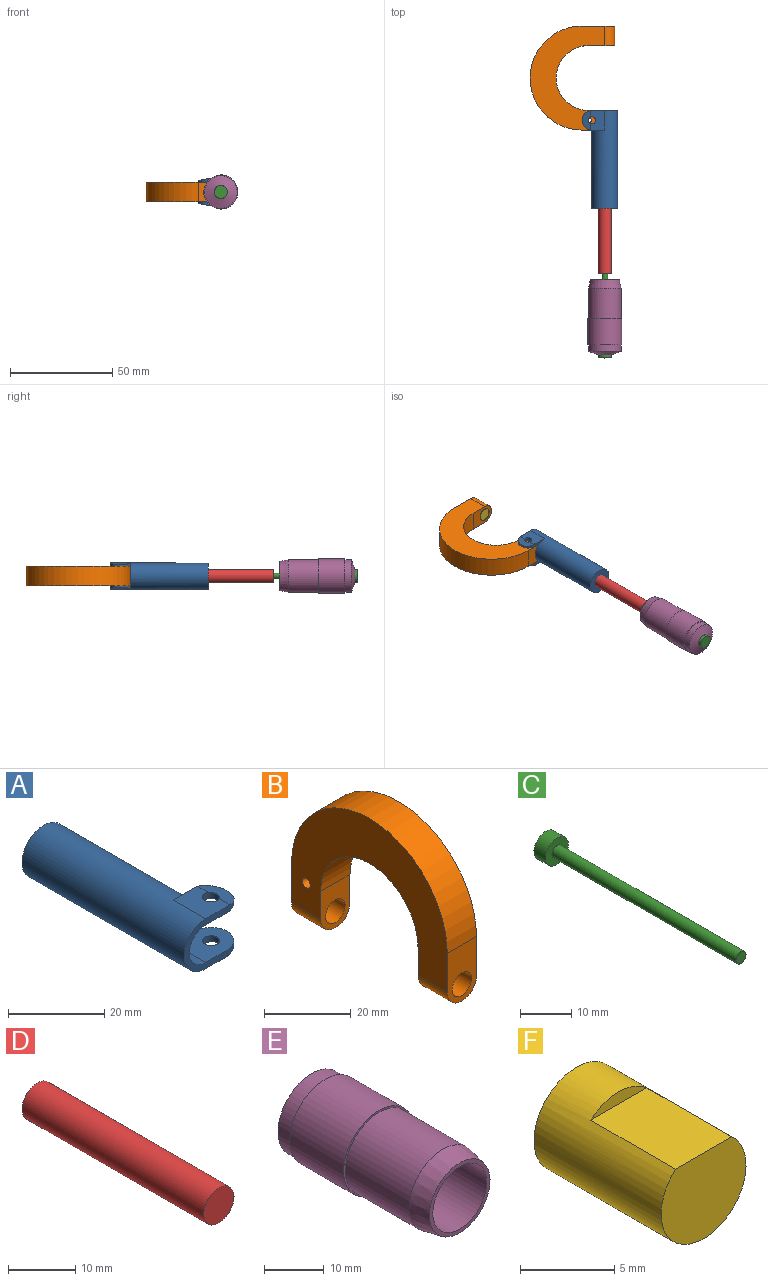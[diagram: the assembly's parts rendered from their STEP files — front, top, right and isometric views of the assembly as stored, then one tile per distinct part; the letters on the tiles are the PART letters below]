
ASSEMBLY  parts=6 mates=6
PART A: 20 faces, bbox 17.5x47.6x12.7 mm
  f0: cylinder r=3.17mm len=31.75mm, axis (0,-1,0), area 633.4mm2, adj f4,f7
  f1: plane 6.35x1.59mm, normal (0,1,0), area 5.5mm2, adj f6,f10,f12,f16
  f2: plane 12.7x12.7mm, normal (0,1,0), area 122.2mm2, adj f3,f6
  f3: cylinder r=1.19mm len=6.35mm, axis (0,-1,0), area 47.5mm2, adj f2,f4
  f4: plane 6.35x6.35mm, normal (0,-1,0), area 27.2mm2, adj f0,f3
  f5: plane 6.35x1.59mm, normal (0,1,0), area 5.5mm2, adj f6,f9,f14,f17
  f6: cylinder r=6.35mm len=47.63mm, axis (0,-1,0), area 1710.1mm2, adj f1,f2,f5,f7,f9,f10,f15
  f7: plane 11.11x9.53mm, normal (0,-1,0), area 58.2mm2, adj f0,f6,f12,f13,f14
  f8: plane 9.4x3.99mm, normal (0.2,0,-0.98), area 26.6mm2, adj f9,f17,f18
  f9: plane 9.53x7.12mm, normal (0,0,-1), area 60.4mm2, adj f5,f6,f8,f15,f17,f18
  f10: plane 9.53x7.12mm, normal (0,0,1), area 60.4mm2, adj f1,f6,f11,f15,f16,f19
  f11: plane 9.4x3.99mm, normal (0.2,0,0.98), area 26.6mm2, adj f10,f16,f19
  f12: plane 11.11x9.53mm, normal (0,0,-1), area 86.5mm2, adj f1,f7,f13,f15,f16,f19
  f13: cylinder r=4.76mm len=9.53mm, axis (0,-1,0), area 142.5mm2, adj f7,f12,f14,f15
  f14: plane 11.11x9.53mm, normal (0,0,1), area 86.5mm2, adj f5,f7,f13,f15,f17,f18
  f15: plane 12.7x12.7mm, normal (0,-1,0), area 47.9mm2, adj f6,f9,f10,f12,f13,f14,f16,f17
  f16: cylinder r=4.76mm len=9.53mm, axis (0,0,-1), area 16.9mm2, adj f1,f10,f11,f12,f15
  f17: cylinder r=4.76mm len=9.53mm, axis (0,0,-1), area 16.9mm2, adj f5,f8,f9,f14,f15
  f18: cylinder r=1.75mm len=3.51mm, axis (0,0,1), area 17mm2, adj f8,f9,f14
  f19: cylinder r=1.75mm len=3.51mm, axis (0,0,1), area 17mm2, adj f10,f11,f12
PART B: 15 faces, bbox 9.5x50.8x41.3 mm
  f0: plane 12.7x9.53mm, normal (0,-1,0), area 79.6mm2, adj f2,f3,f4,f11,f12
  f1: plane 12.7x9.53mm, normal (0,1,0), area 79.6mm2, adj f2,f3,f4,f9,f10
  f2: plane 50.8x36.51mm, normal (-1,0,0), area 924.3mm2, adj f0,f1,f4,f5,f6,f7,f8,f10
  f3: plane 50.8x36.51mm, normal (1,0,0), area 924.3mm2, adj f0,f1,f4,f5,f6,f7,f8,f10
  f4: cylinder r=15.88mm len=31.75mm, axis (-1,0,0), area 475mm2, adj f0,f1,f2,f3
  f5: plane 15.88x9.53mm, normal (0,1,0), area 109.8mm2, adj f2,f3,f6,f11,f12
  f6: cylinder r=25.4mm len=50.8mm, axis (-1,0,0), area 760.1mm2, adj f2,f3,f5,f7
  f7: plane 15.88x9.53mm, normal (0,-1,0), area 109.8mm2, adj f2,f3,f6,f9,f10
  f8: cylinder r=1.35mm len=9.53mm, axis (-1,0,0), area 80.9mm2, adj f2,f3
  f9: cylinder r=3.17mm len=9.53mm, axis (0,1,0), area 185.5mm2, adj f1,f7,f13
  f10: cylinder r=4.76mm len=9.53mm, axis (0,1,0), area 142.5mm2, adj f1,f2,f3,f7
  f11: cylinder r=3.17mm len=9.53mm, axis (0,1,0), area 190mm2, adj f0,f5
  f12: cylinder r=4.76mm len=9.53mm, axis (0,1,0), area 142.5mm2, adj f0,f2,f3,f5
  f13: cylinder r=1.19mm len=4.99mm, axis (0,0,1), area 36.5mm2, adj f9,f14
  f14: plane 2.38x2.38mm, normal (0,0,-1), area 4.5mm2, adj f13
PART C: 5 faces, bbox 6.4x54x6.4 mm
  f0: cylinder r=1.39mm len=50.8mm, axis (0,1,0), area 443.4mm2, adj f1,f4
  f1: plane 2.78x2.78mm, normal (0,-1,0), area 6.1mm2, adj f0
  f2: cylinder r=3.17mm len=6.35mm, axis (0,-1,0), area 63.3mm2, adj f3,f4
  f3: plane 6.35x6.35mm, normal (0,1,0), area 31.7mm2, adj f2
  f4: plane 6.35x6.35mm, normal (0,-1,0), area 25.6mm2, adj f0,f2
PART D: 5 faces, bbox 6.4x38.1x6.4 mm
  f0: cylinder r=3.17mm len=38.1mm, axis (0,1,0), area 760.1mm2, adj f1,f2
  f1: plane 6.35x6.35mm, normal (0,-1,0), area 31.7mm2, adj f0
  f2: plane 6.35x6.35mm, normal (0,1,0), area 27.2mm2, adj f0,f3
  f3: cylinder r=1.19mm len=12.7mm, axis (0,1,0), area 95mm2, adj f2,f4
  f4: plane 2.38x2.38mm, normal (0,1,0), area 4.5mm2, adj f3
PART E: 13 faces, bbox 16.7x36.5x16.7 mm
  f0: plane 12.7x12.7mm, normal (0,-1,0), area 122.2mm2, adj f1,f12
  f1: cylinder r=6.35mm len=31.75mm, axis (0,-1,0), area 1266.8mm2, adj f0,f2
  f2: plane 14.29x14.29mm, normal (0,-1,0), area 33.6mm2, adj f1,f3
  f3: cone r=7.14mm half-angle=11.3deg, axis (0,1,0), area 192.8mm2, adj f2,f4
  f4: cylinder r=7.94mm len=15.88mm, axis (0,-1,0), area 751.1mm2, adj f3,f5
  f5: plane 16.67x16.67mm, normal (0,-1,0), area 20.3mm2, adj f4,f6
  f6: cylinder r=8.33mm len=16.67mm, axis (0,-1,0), area 665.1mm2, adj f5,f7
  f7: plane 16.67x16.67mm, normal (0,1,0), area 20.3mm2, adj f6,f8
  f8: cylinder r=7.94mm len=15.88mm, axis (0,-1,0), area 158.3mm2, adj f7,f9
  f9: cone r=7.94mm half-angle=71.6deg, axis (0,-1,0), area 175.3mm2, adj f8,f10
  f10: cylinder r=3.17mm len=6.35mm, axis (0,-1,0), area 31.7mm2, adj f9,f11
  f11: plane 6.35x6.35mm, normal (0,1,0), area 27.2mm2, adj f10,f12
  f12: cylinder r=1.19mm len=3.18mm, axis (0,-1,0), area 23.8mm2, adj f0,f11
PART F: 5 faces, bbox 6.4x9.5x6.4 mm
  f0: cylinder r=3.17mm len=9.53mm, axis (0,1,0), area 160.9mm2, adj f1,f2,f3,f4
  f1: plane 6.35x5.56mm, normal (0,-1,0), area 29.4mm2, adj f0,f3
  f2: plane 6.35x6.35mm, normal (0,1,0), area 31.7mm2, adj f0
  f3: plane 6.35x4.2mm, normal (0,0,1), area 26.7mm2, adj f0,f1,f4
  f4: plane 4.2x0.79mm, normal (0,-1,0), area 2.3mm2, adj f0,f3
PLACE A rot(axis=(0,0,-1),180deg) t=(0,-31.75,0)mm
PLACE B rot(axis=(-0.71,0,0.71),180deg) t=(-7.94,-15.88,4.76)mm
PLACE C rot(axis=(0.16,0,-0.99),180deg) t=(0,-149.34,0)mm
PLACE D rot(axis=(0.16,0,-0.99),180deg) t=(0,-111.24,0)mm
PLACE E rot(axis=(-0.59,0,-0.81),180deg) t=(0,-114.42,0)mm
PLACE F rot(axis=(0,1,0),90deg) t=(0,9.52,0)mm
MATE cylindrical B.f9 <-> C.f0  axis (0,1,0) through (0,-31.75,0)mm
MATE slider D.f3 <-> C.f0  axis (0,-1,0) through (0,-104.89,0)mm
MATE planar D.f3 <-> C.f0  axis (0,-1,0) through (0,-98.54,0)mm
MATE slider E.f1 <-> C.f0  axis (0,1,0) through (0,-149.34,0)mm
MATE planar E.f1 <-> C.f2  axis (0,-1,0) through (0,-149.34,0)mm
MATE fastened A.f0 <-> B.f9  axis (0,1,0) through (0,-41.27,0)mm
